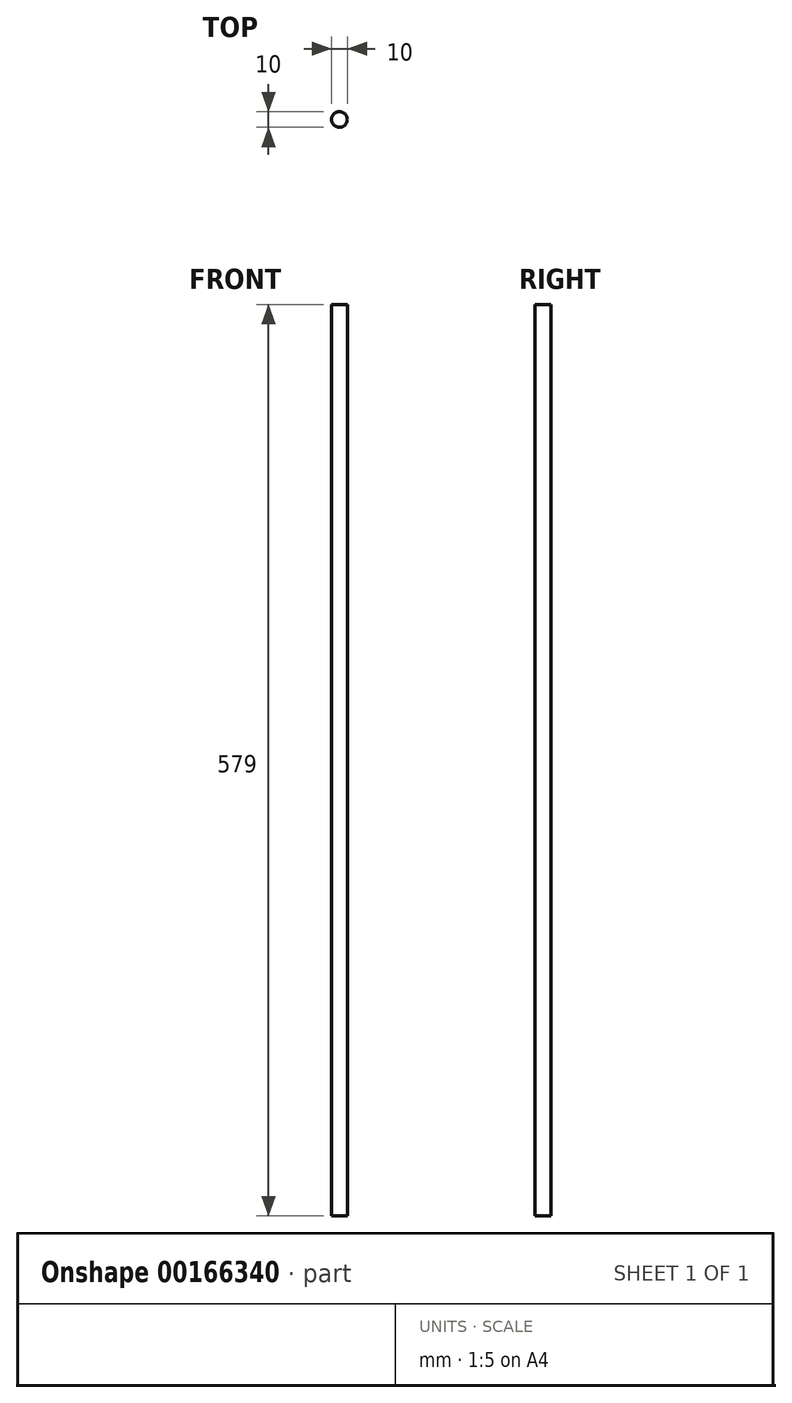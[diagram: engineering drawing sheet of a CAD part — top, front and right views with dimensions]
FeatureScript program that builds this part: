
annotation { "Feature Type Name" : "Feature", "Feature Type Description" : "" }
export const myFeature = defineFeature(function(context is Context, id is Id, definition is map)
    precondition{}
    {
        {
            var Q0;
            Q0=qCreatedBy(makeId("Top.planeOp"),FACE);
            var sketch = newSketch(context, id + "F0", { "sketchPlane" : qUnion([Q0])});
            skCircle(sketch, "E0", {"center": v(0, 0) * mm, "radius": 5 * mm});
            skSolve(sketch);
        }
        {
            var Q0;
            Q0=qSketchRegion(id+"F0",true);
            extrude(context, id + "F1", {"entities" : qUnion([Q0]), "depth" : 579 * mm});
        }
    });
